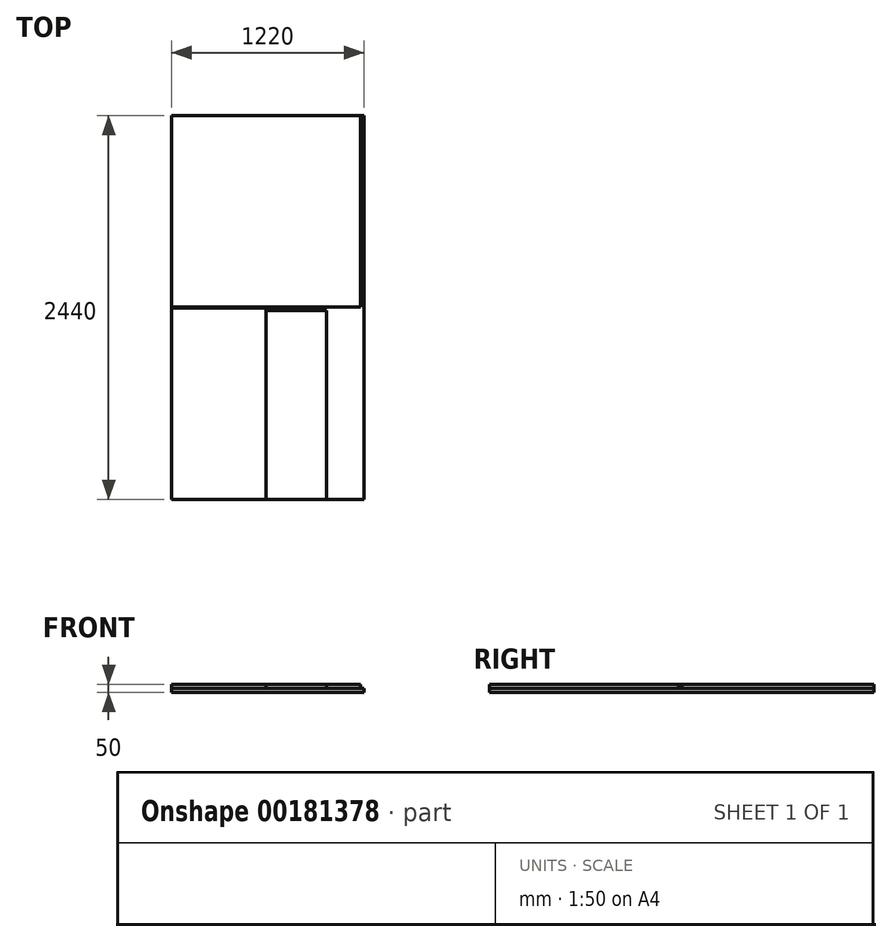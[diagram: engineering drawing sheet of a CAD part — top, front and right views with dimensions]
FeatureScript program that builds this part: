
annotation { "Feature Type Name" : "Feature", "Feature Type Description" : "" }
export const myFeature = defineFeature(function(context is Context, id is Id, definition is map)
    precondition{}
    {
        {
            var Q0;
            Q0=qCreatedBy(makeId("Top.planeOp"),FACE);
            var sketch = newSketch(context, id + "F0", { "sketchPlane" : qUnion([Q0])});
            skLineSegment(sketch, "E0.bottom", {"start": v(0, 0) * mm, "end": v(600, 0) * mm});
            skLineSegment(sketch, "E0.top", {"start": v(0, 1218) * mm, "end": v(600, 1218) * mm});
            skLineSegment(sketch, "E0.left", {"start": v(0, 0) * mm, "end": v(0, 1218) * mm});
            skLineSegment(sketch, "E0.right", {"start": v(600, 0) * mm, "end": v(600, 1218) * mm});
            skSolve(sketch);
        }
        {
            var Q0;
            Q0 = qSketchRegion(id + "F0", true);
            extrude(context, id + "F1", {"entities" : qUnion([Q0]), "depth" : 25 * mm});
        }
        {
            var Q0;
            Q0=makeQuery(id+"F1.opExtrude","CAP_FACE",FACE,{"disambiguationData":[OSD([sQuery(id+"F0.wireOp",EDGE,"E0.bottom"),sQuery(id+"F0.wireOp",EDGE,"E0.top"),sQuery(id+"F0.wireOp",EDGE,"E0.left"),sQuery(id+"F0.wireOp",EDGE,"E0.right")])],"isStart":true});
            var sketch = newSketch(context, id + "F2", { "sketchPlane" : qUnion([Q0])});
            skLineSegment(sketch, "E1.bottom", {"start": v(0, 0) * mm, "end": v(1220, 0) * mm});
            skLineSegment(sketch, "E1.top", {"start": v(0, -2440) * mm, "end": v(1220, -2440) * mm});
            skLineSegment(sketch, "E1.left", {"start": v(0, 0) * mm, "end": v(0, -2440) * mm});
            skLineSegment(sketch, "E1.right", {"start": v(1220, 0) * mm, "end": v(1220, -2440) * mm});
            skSolve(sketch);
        }
        {
            var Q0;
            Q0 = qSketchRegion(id + "F2", true);
            extrude(context, id + "F3", {"entities" : qUnion([Q0]), "depth" : 25 * mm});
        }
        {
            var Q0;
            Q0=makeQuery(id+"F3.opExtrude","CAP_FACE",FACE,{"disambiguationData":[OSD([sQuery(id+"F2.wireOp",EDGE,"E1.bottom"),sQuery(id+"F2.wireOp",EDGE,"E1.top"),sQuery(id+"F2.wireOp",EDGE,"E1.left"),sQuery(id+"F2.wireOp",EDGE,"E1.right")])],"isStart":true});
            var sketch = newSketch(context, id + "F4", { "sketchPlane" : qUnion([Q0])});
            skLineSegment(sketch, "E2.bottom", {"start": v(0, 1222) * mm, "end": v(1200, 1222) * mm});
            skLineSegment(sketch, "E2.top", {"start": v(0, 2440) * mm, "end": v(1200, 2440) * mm});
            skLineSegment(sketch, "E2.left", {"start": v(0, 1222) * mm, "end": v(0, 2440) * mm});
            skLineSegment(sketch, "E2.right", {"start": v(1200, 1222) * mm, "end": v(1200, 2440) * mm});
            skSolve(sketch);
        }
        {
            var Q0;
            Q0 = qSketchRegion(id + "F4", true);
            extrude(context, id + "F5", {"entities" : qUnion([Q0]), "depth" : 25 * mm});
        }
        {
            var Q0;
            Q0=makeQuery(id+"F3.opExtrude","CAP_FACE",FACE,{"disambiguationData":[OSD([sQuery(id+"F2.wireOp",EDGE,"E1.bottom"),sQuery(id+"F2.wireOp",EDGE,"E1.top"),sQuery(id+"F2.wireOp",EDGE,"E1.left"),sQuery(id+"F2.wireOp",EDGE,"E1.right")])],"isStart":true});
            var sketch = newSketch(context, id + "F6", { "sketchPlane" : qUnion([Q0])});
            skLineSegment(sketch, "E3.bottom", {"start": v(600, 0) * mm, "end": v(982, 0) * mm});
            skLineSegment(sketch, "E3.top", {"start": v(600, 1200) * mm, "end": v(982, 1200) * mm});
            skLineSegment(sketch, "E3.left", {"start": v(600, 0) * mm, "end": v(600, 1200) * mm});
            skLineSegment(sketch, "E3.right", {"start": v(982, 0) * mm, "end": v(982, 1200) * mm});
            skSolve(sketch);
        }
        {
            var Q0;
            Q0 = qSketchRegion(id + "F6", true);
            extrude(context, id + "F7", {"entities" : qUnion([Q0]), "depth" : 25 * mm});
        }
    });
